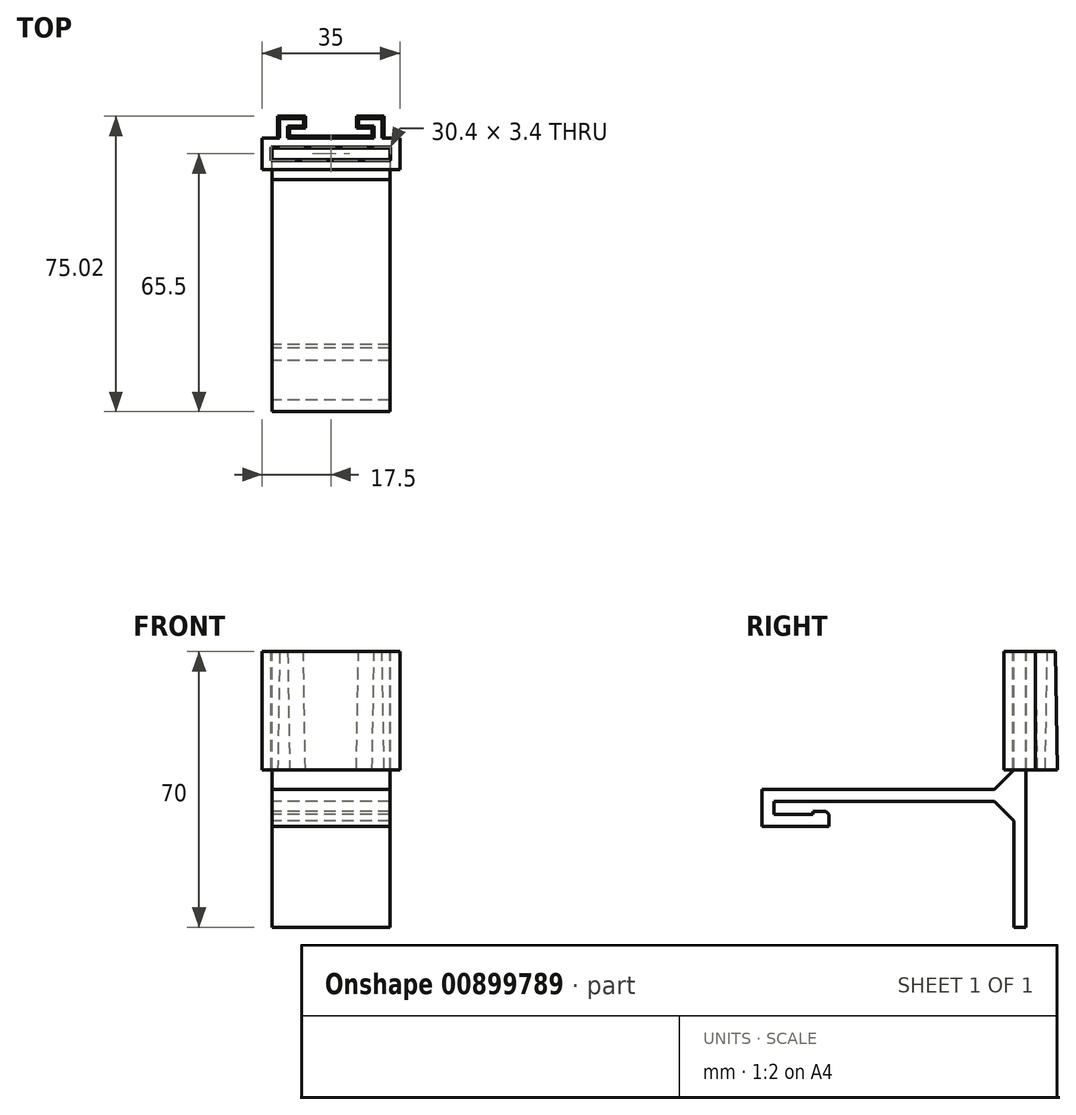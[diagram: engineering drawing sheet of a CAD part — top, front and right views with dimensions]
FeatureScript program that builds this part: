
annotation { "Feature Type Name" : "Feature", "Feature Type Description" : "" }
export const myFeature = defineFeature(function(context is Context, id is Id, definition is map)
    precondition{}
    {
        {
            var Q0;
            Q0=qCreatedBy(makeId("Right.planeOp"),FACE);
            var sketch = newSketch(context, id + "F0", { "sketchPlane" : qUnion([Q0])});
            skLineSegment(sketch, "E0.bottom", {"start": v(0, 0) * mm, "end": v(64, 0) * mm});
            skLineSegment(sketch, "E0.top", {"start": v(0, -3) * mm, "end": v(64, -3) * mm});
            skLineSegment(sketch, "E0.left", {"start": v(0, 0) * mm, "end": v(0, -3) * mm});
            skLineSegment(sketch, "E0.right", {"start": v(64, 0) * mm, "end": v(64, -3) * mm});
            skLineSegment(sketch, "E1.bottom", {"start": v(64, 0) * mm, "end": v(67, 0) * mm});
            skLineSegment(sketch, "E1.top", {"start": v(64, -35) * mm, "end": v(67, -35) * mm});
            skLineSegment(sketch, "E1.left", {"start": v(64, 0) * mm, "end": v(64, -35) * mm});
            skLineSegment(sketch, "E1.right", {"start": v(67, 0) * mm, "end": v(67, -35) * mm});
            skLineSegment(sketch, "E2.bottom", {"start": v(0, -3) * mm, "end": v(3, -3) * mm});
            skLineSegment(sketch, "E2.top", {"start": v(0, -9.4) * mm, "end": v(3, -9.4) * mm});
            skLineSegment(sketch, "E2.left", {"start": v(0, -3) * mm, "end": v(0, -9.4) * mm});
            skLineSegment(sketch, "E2.right", {"start": v(3, -3) * mm, "end": v(3, -9.4) * mm});
            skLineSegment(sketch, "E3.bottom", {"start": v(3, -9.4) * mm, "end": v(17, -9.4) * mm});
            skLineSegment(sketch, "E3.top", {"start": v(3, -6.4) * mm, "end": v(17, -6.4) * mm});
            skLineSegment(sketch, "E3.left", {"start": v(3, -9.4) * mm, "end": v(3, -6.4) * mm});
            skLineSegment(sketch, "E3.right", {"start": v(17, -9.4) * mm, "end": v(17, -6.4) * mm});
            skLineSegment(sketch, "E4.top", {"start": v(64, 35) * mm, "end": v(67, 35) * mm});
            skLineSegment(sketch, "E4.left", {"start": v(64, 0) * mm, "end": v(64, 35) * mm});
            skLineSegment(sketch, "E4.right", {"start": v(67, 0) * mm, "end": v(67, 35) * mm});
            skLineSegment(sketch, "E5.bottom", {"start": v(64, 0) * mm, "end": v(59, 0) * mm});
            skLineSegment(sketch, "E5.top", {"start": v(64, 5) * mm, "end": v(59, 5) * mm});
            skLineSegment(sketch, "E5.left", {"start": v(64, 0) * mm, "end": v(64, 5) * mm});
            skLineSegment(sketch, "E5.right", {"start": v(59, 0) * mm, "end": v(59, 5) * mm});
            skLineSegment(sketch, "E6.bottom", {"start": v(17, -6.4) * mm, "end": v(13, -6.4) * mm});
            skLineSegment(sketch, "E6.top", {"start": v(17, -5.6) * mm, "end": v(13, -5.6) * mm});
            skLineSegment(sketch, "E6.left", {"start": v(17, -6.4) * mm, "end": v(17, -5.6) * mm});
            skLineSegment(sketch, "E6.right", {"start": v(13, -6.4) * mm, "end": v(13, -5.6) * mm});
            skLineSegment(sketch, "E7.bottom", {"start": v(64, -3) * mm, "end": v(59, -3) * mm});
            skLineSegment(sketch, "E7.top", {"start": v(64, -8) * mm, "end": v(59, -8) * mm});
            skLineSegment(sketch, "E7.left", {"start": v(64, -3) * mm, "end": v(64, -8) * mm});
            skLineSegment(sketch, "E7.right", {"start": v(59, -3) * mm, "end": v(59, -8) * mm});
            skSolve(sketch);
        }
        {
            var Q0;
            Q0=qSketchRegion(id+"F0",true);
            extrude(context, id + "F1", {"entities" : qUnion([Q0]), "depth" : 30 * mm, "offsetDistance" : 25 * mm});
        }
        {
            var Q0;
            Q0=qCreatedBy(makeId("Top.planeOp"),FACE);
            cPlane(context, id + "F2", {"entities" : qUnion([Q0]), "cplaneType" : CPlaneType.OFFSET, "offset" : 35 * mm, "width" : 150 * mm, "height" : 150 * mm});
        }
        {
            var Q0;
            Q0=qCreatedBy(id+"F2.planeOp",FACE);
            var sketch = newSketch(context, id + "F3", { "sketchPlane" : qUnion([Q0])});
            skLineSegment(sketch, "E8.0.0", {"start": v(0, 67) * mm, "end": v(0, 64) * mm, "construction": true});
            skLineSegment(sketch, "E8.0.1", {"start": v(0, 64) * mm, "end": v(30, 64) * mm, "construction": true});
            skLineSegment(sketch, "E8.0.2", {"start": v(30, 64) * mm, "end": v(30, 67) * mm, "construction": true});
            skLineSegment(sketch, "E8.0.3", {"start": v(30, 67) * mm, "end": v(0, 67) * mm, "construction": true});
            skLineSegment(sketch, "E9", {"start": v(15, 67) * mm, "end": v(15, 64) * mm, "construction": true});
            skLineSegment(sketch, "E10", {"start": v(0, 65.5) * mm, "end": v(30, 65.5) * mm, "construction": true});
            skLineSegment(sketch, "E11.bottom", {"start": v(-0.2, 67.2) * mm, "end": v(30.2, 67.2) * mm});
            skLineSegment(sketch, "E11.top", {"start": v(-0.2, 63.8) * mm, "end": v(30.2, 63.8) * mm});
            skLineSegment(sketch, "E11.left", {"start": v(-0.2, 67.2) * mm, "end": v(-0.2, 63.8) * mm});
            skLineSegment(sketch, "E11.right", {"start": v(30.2, 67.2) * mm, "end": v(30.2, 63.8) * mm});
            skPoint(sketch, "E11.middle", {"position": v(15, 65.5) * mm});
            skLineSegment(sketch, "E12.bottom", {"start": v(-2.5, 69.5) * mm, "end": v(32.5, 69.5) * mm});
            skLineSegment(sketch, "E12.top", {"start": v(-2.5, 61.5) * mm, "end": v(32.5, 61.5) * mm});
            skLineSegment(sketch, "E12.left", {"start": v(-2.5, 69.5) * mm, "end": v(-2.5, 61.5) * mm});
            skLineSegment(sketch, "E12.right", {"start": v(32.5, 69.5) * mm, "end": v(32.5, 61.5) * mm});
            skPoint(sketch, "E13.middle.positionSnap0", {"position": v(15, 61.5) * mm});
            skPoint(sketch, "E13.centerSnap0", {"position": v(15, 61.5) * mm});
            skLineSegment(sketch, "E14.bottom", {"start": v(2, 69.5) * mm, "end": v(4, 69.5) * mm});
            skLineSegment(sketch, "E14.top", {"start": v(2, 72.5) * mm, "end": v(4, 72.5) * mm});
            skLineSegment(sketch, "E14.left", {"start": v(2, 69.5) * mm, "end": v(2, 72.5) * mm});
            skLineSegment(sketch, "E14.right", {"start": v(4, 69.5) * mm, "end": v(4, 72.5) * mm});
            skLineSegment(sketch, "E15.bottom", {"start": v(26, 69.5) * mm, "end": v(28, 69.5) * mm});
            skLineSegment(sketch, "E15.top", {"start": v(26, 72.5) * mm, "end": v(28, 72.5) * mm});
            skLineSegment(sketch, "E15.left", {"start": v(26, 69.5) * mm, "end": v(26, 72.5) * mm});
            skLineSegment(sketch, "E15.right", {"start": v(28, 69.5) * mm, "end": v(28, 72.5) * mm});
            skLineSegment(sketch, "E16.bottom", {"start": v(2, 72.5) * mm, "end": v(8, 72.5) * mm});
            skLineSegment(sketch, "E16.top", {"start": v(2, 74.5) * mm, "end": v(8, 74.5) * mm});
            skLineSegment(sketch, "E16.left", {"start": v(2, 72.5) * mm, "end": v(2, 74.5) * mm});
            skLineSegment(sketch, "E16.right", {"start": v(8, 72.5) * mm, "end": v(8, 74.5) * mm});
            skLineSegment(sketch, "E17.bottom", {"start": v(28, 72.5) * mm, "end": v(22, 72.5) * mm});
            skLineSegment(sketch, "E17.top", {"start": v(28, 74.5) * mm, "end": v(22, 74.5) * mm});
            skLineSegment(sketch, "E17.left", {"start": v(28, 72.5) * mm, "end": v(28, 74.5) * mm});
            skLineSegment(sketch, "E17.right", {"start": v(22, 72.5) * mm, "end": v(22, 74.5) * mm});
            skLineSegment(sketch, "E18.bottom", {"start": v(2, 69.5) * mm, "end": v(28, 69.5) * mm});
            skLineSegment(sketch, "E18.top", {"start": v(2, 68.5) * mm, "end": v(28, 68.5) * mm});
            skLineSegment(sketch, "E18.left", {"start": v(2, 69.5) * mm, "end": v(2, 68.5) * mm});
            skLineSegment(sketch, "E18.right", {"start": v(28, 69.5) * mm, "end": v(28, 68.5) * mm});
            skSolve(sketch);
        }
        {
            var Q0;
            Q0=makeQuery(id+"F3.imprint","IMPRINT",FACE,{"disambiguationData":[TD([[makeQuery(id+"F3.imprint","IMPRINT",EDGE,{"derivedFrom":sQuery(id+"F3.wireOp",EDGE,"E11.bottom")}),1.0]])]});
            var Q1;
            Q1=makeQuery(id+"F3.imprint","IMPRINT",FACE,{"disambiguationData":[TD([[makeQuery(id+"F3.imprint","IMPRINT",EDGE,{"derivedFrom":sQuery(id+"F3.wireOp",EDGE,"E18.top")}),1.0]])]});
            extrude(context, id + "F4", {"entities" : qUnion([Q0, Q1]), "oppositeDirection" : true, "depth" : 30 * mm, "offsetDistance" : 25 * mm});
        }
        {
            var Q0;
            Q0=makeQuery(id+"F1.opExtrude","SWEPT_EDGE",EDGE,{"disambiguationData":[OSD([sQuery(id+"F0.wireOp",EDGE,"E6.top"),sQuery(id+"F0.wireOp",EDGE,"E6.left")])]});
            chamfer(context, id + "F5", {"entities" : qUnion([Q0]), "width" : 0.8 * mm, "tangentPropagation" : true});
        }
        {
            var Q0;
            Q0=makeQuery(id+"F1.opExtrude","SWEPT_EDGE",EDGE,{"disambiguationData":[OSD([sQuery(id+"F0.wireOp",EDGE,"E5.top"),sQuery(id+"F0.wireOp",EDGE,"E5.right")])]});
            var Q1;
            Q1=makeQuery(id+"F1.opExtrude","SWEPT_EDGE",EDGE,{"disambiguationData":[OSD([sQuery(id+"F0.wireOp",EDGE,"E7.top"),sQuery(id+"F0.wireOp",EDGE,"E7.right")])]});
            chamfer(context, id + "F6", {"entities" : qUnion([Q0, Q1]), "width" : 5 * mm, "tangentPropagation" : true});
        }
        {
            var Q0;
            Q0=makeQuery(id+"F3.imprint","IMPRINT",FACE,{"disambiguationData":[TD([[makeQuery(id+"F3.imprint","IMPRINT",EDGE,{"derivedFrom":sQuery(id+"F3.wireOp",EDGE,"E17.top")}),1.0]])]});
            var Q1;
            {var subQ0=sQuery(id+"F3.wireOp",EDGE,"E15.left");Q1=makeQuery(id+"F3.imprint","IMPRINT",FACE,{"disambiguationData":[TD([[makeQuery(id+"F3.imprint","IMPRINT",EDGE,{"derivedFrom":subQ0}),-1.0]])]});}
            var Q2;
            Q2=makeQuery(id+"F3.imprint","IMPRINT",FACE,{"disambiguationData":[TD([[makeQuery(id+"F3.imprint","IMPRINT",EDGE,{"derivedFrom":sQuery(id+"F3.wireOp",EDGE,"E18.top")}),1.0]])]});
            var Q3;
            Q3=makeQuery(id+"F3.imprint","IMPRINT",FACE,{"disambiguationData":[TD([[makeQuery(id+"F3.imprint","IMPRINT",EDGE,{"derivedFrom":sQuery(id+"F3.wireOp",EDGE,"E16.top")}),-1.0]])]});
            var Q4;
            {var subQ0=sQuery(id+"F3.wireOp",EDGE,"E14.left");Q4=makeQuery(id+"F3.imprint","IMPRINT",FACE,{"disambiguationData":[TD([[makeQuery(id+"F3.imprint","IMPRINT",EDGE,{"derivedFrom":subQ0}),-1.0]])]});}
            extrude(context, id + "F7", {"entities" : qUnion([Q0, Q1, Q2, Q3, Q4]), "operationType" : NewBodyOperationType.ADD, "oppositeDirection" : true, "depth" : 30 * mm, "offsetDistance" : 25 * mm, "hasDraft" : true, "draftAngle" : 1 * degree});
        }
    });
